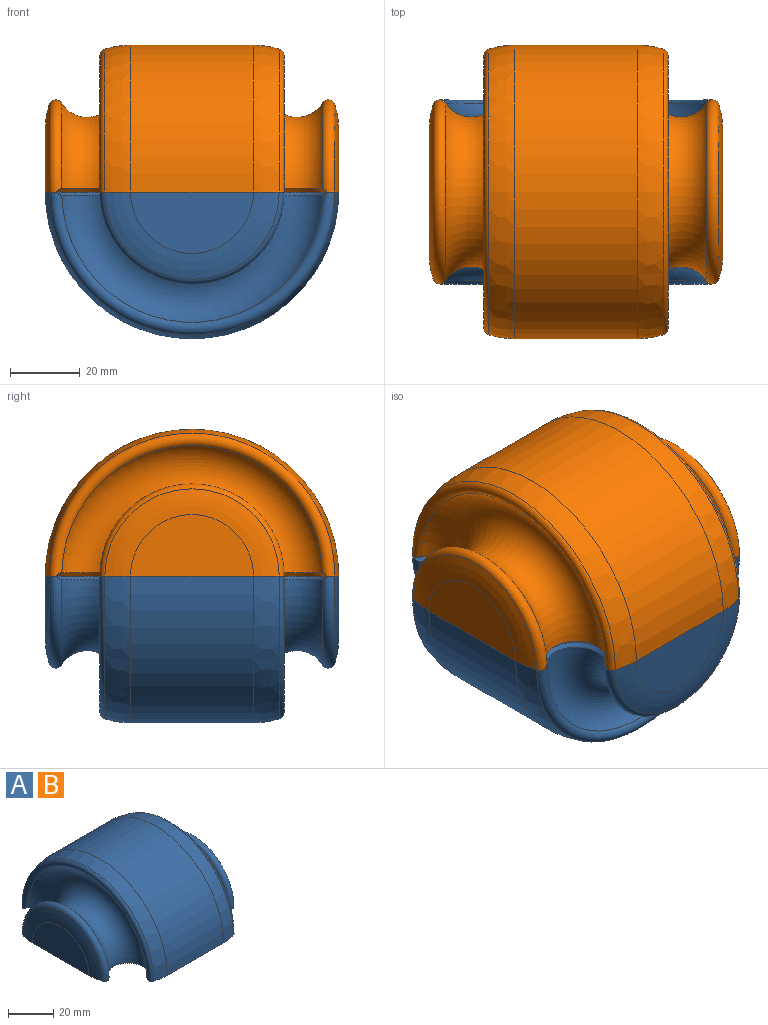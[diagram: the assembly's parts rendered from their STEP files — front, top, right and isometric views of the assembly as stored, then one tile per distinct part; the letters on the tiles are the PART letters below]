
ASSEMBLY  parts=2 mates=1
PART A: 28 faces, bbox 84x88.7x44.3 mm
  f0: plane 35.13x17.57mm, normal (1,0,0), area 484.7mm2, adj f1,f9
  f1: torus R=17.57mm, axis (-1,0,0), area 500.2mm2, adj f0,f9,f16
  f2: torus R=30mm, axis (-1,0,0), area 2520.6mm2, adj f10,f11,f16,f17
  f3: torus R=17.57mm, axis (-1,0,0), area 978.4mm2, adj f4,f9,f17
  f4: cylinder r=42mm len=84mm, axis (-1,0,0), area 4635.8mm2, adj f3,f5,f9
  f5: torus R=17.57mm, axis (-1,0,0), area 978.4mm2, adj f4,f9,f14
  f6: torus R=30mm, axis (-1,0,0), area 2521.3mm2, adj f12,f13,f14,f15
  f7: torus R=17.57mm, axis (-1,0,0), area 500.2mm2, adj f8,f9,f15
  f8: plane 35.13x17.57mm, normal (-1,0,0), area 484.7mm2, adj f7,f9
  f9: plane 84.02x84.02mm, normal (0,0,-1), area 5393.5mm2, adj f0,f1,f3,f4,f5,f7,f8,f10
  f10: bspline ~18.48x18.48mm, area 48.9mm2, adj f2,f9,f16,f17
  f11: bspline ~18.48x18.48mm, area 48.9mm2, adj f2,f9,f16,f17
  f12: bspline ~18.48x18.48mm, area 48.9mm2, adj f6,f9,f14,f15
  f13: bspline ~18.48x18.48mm, area 48.9mm2, adj f6,f9,f14,f15
  f14: torus R=38.96mm, axis (1,0,0), area 556.9mm2, adj f5,f6,f9,f12,f13
  f15: torus R=24.33mm, axis (1,0,0), area 367.7mm2, adj f6,f7,f9,f12,f13
  f16: torus R=24.33mm, axis (1,0,0), area 367.8mm2, adj f1,f2,f9,f10,f11
  f17: torus R=38.96mm, axis (1,0,0), area 556.9mm2, adj f2,f3,f9,f10,f11
  f18: cylinder r=2.5mm len=5mm, axis (0,0,-1), area 39.3mm2, adj f9,f19
  f19: plane 5x5mm, normal (0,0,-1), area 19.6mm2, adj f18
  f20: cylinder r=2.5mm len=5mm, axis (0,0,-1), area 39.3mm2, adj f9,f21
  f21: plane 5x5mm, normal (0,0,-1), area 19.6mm2, adj f20
  f22: cylinder r=2.5mm len=5mm, axis (0,0,-1), area 39.3mm2, adj f9,f23
  f23: plane 5x5mm, normal (0,0,-1), area 19.6mm2, adj f22
  f24: cylinder r=2.5mm len=5mm, axis (0,0,-1), area 39.3mm2, adj f9,f25
  f25: plane 5x5mm, normal (0,0,-1), area 19.6mm2, adj f24
  f26: cylinder r=2.5mm len=16mm, axis (0,0,-1), area 251.3mm2, adj f9,f27
  f27: plane 5x5mm, normal (0,0,-1), area 19.6mm2, adj f26
PART B: same geometry as A
PLACE A rot(axis=(-0.71,-0.71,0),180deg) t=(42,0,0)mm
PLACE B t=(42,0,0)mm
MATE revolute A.f26 <-> B.f26  axis (0,0,1) through (42,0,0)mm
